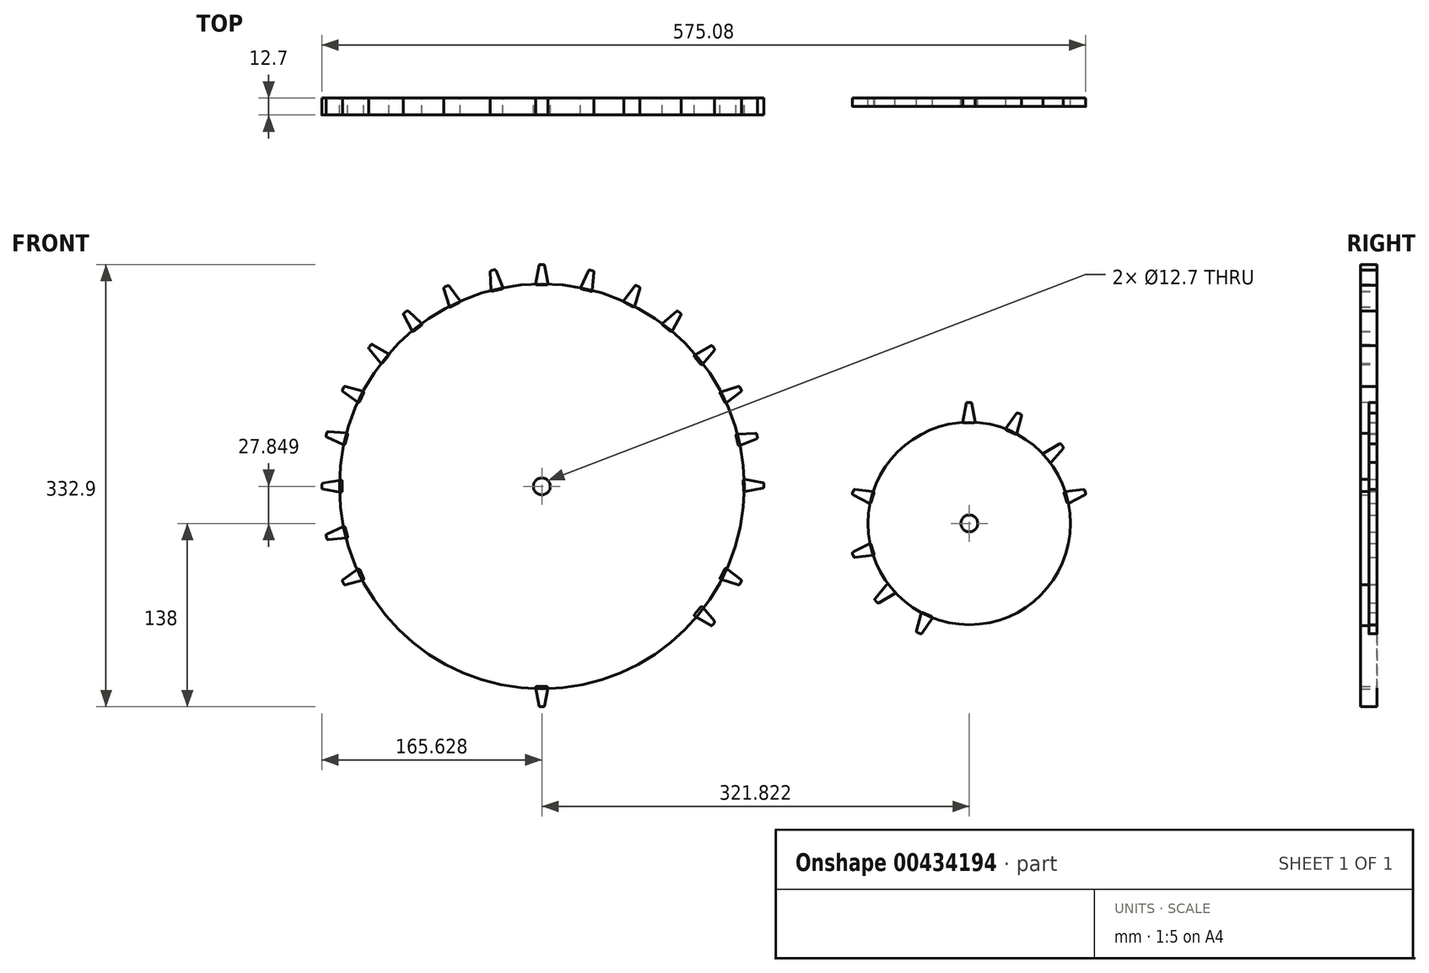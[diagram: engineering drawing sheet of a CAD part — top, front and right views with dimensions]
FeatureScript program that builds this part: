
annotation { "Feature Type Name" : "Feature", "Feature Type Description" : "" }
export const myFeature = defineFeature(function(context is Context, id is Id, definition is map)
    precondition{}
    {
        {
            var Q0;
            Q0=qCreatedBy(makeId("Front.planeOp"),FACE);
            var sketch = newSketch(context, id + "F0", { "sketchPlane" : qUnion([Q0])});
            skCircle(sketch, "E0", {"center": v(-44.38, 27.85) * mm, "radius": 152.4 * mm});
            skCircle(sketch, "E1", {"center": v(-44.38, 27.85) * mm, "radius": 6.35 * mm});
            skSolve(sketch);
        }
        {
            var Q0;
            Q0=qCreatedBy(makeId("Front.planeOp"),FACE);
            var sketch = newSketch(context, id + "F1", { "sketchPlane" : qUnion([Q0])});
            skCircle(sketch, "E2", {"center": v(277.44, 0) * mm, "radius": 76.2 * mm});
            skCircle(sketch, "E3", {"center": v(277.44, 0) * mm, "radius": 6.35 * mm});
            skSolve(sketch);
        }
        {
            var Q0;
            Q0=qCreatedBy(makeId("Front.planeOp"),FACE);
            var sketch = newSketch(context, id + "F2", { "sketchPlane" : qUnion([Q0])});
            skLineSegment(sketch, "E4.0", {"start": v(-40.88, 179.56) * mm, "end": v(-47.98, 179.5) * mm});
            skLineSegment(sketch, "E4.1", {"start": v(-48.96, 180.66) * mm, "end": v(-46.6, 194.09) * mm});
            skLineSegment(sketch, "E4.2", {"start": v(-45.63, 194.9) * mm, "end": v(-43.24, 194.9) * mm});
            skLineSegment(sketch, "E4.3", {"start": v(-42.27, 194.08) * mm, "end": v(-39.91, 180.72) * mm});
            skPoint(sketch, "E4.0.midPoint", {"position": v(-44.44, 179.53) * mm});
            skArc(sketch, "E5.filletArc", {"start": v(-45.63, 194.9) * mm, "mid": v(-46.26, 194.67) * mm, "end": v(-46.6, 194.09) * mm});
            skArc(sketch, "E6.filletArc", {"start": v(-42.27, 194.08) * mm, "mid": v(-42.6, 194.67) * mm, "end": v(-43.24, 194.9) * mm});
            skArc(sketch, "E7.filletArc", {"start": v(-48.96, 180.66) * mm, "mid": v(-48.74, 179.85) * mm, "end": v(-47.98, 179.5) * mm});
            skArc(sketch, "E8.filletArc", {"start": v(-40.88, 179.56) * mm, "mid": v(-40.12, 179.92) * mm, "end": v(-39.91, 180.72) * mm});
            skLineSegment(sketch, "E9.2.0", {"start": v(70.92, 126.83) * mm, "end": v(82.73, 133.64) * mm});
            skLineSegment(sketch, "E9.2.1", {"start": v(83.97, 133.42) * mm, "end": v(85.5, 131.6) * mm});
            skLineSegment(sketch, "E9.2.2", {"start": v(85.5, 130.32) * mm, "end": v(76.78, 119.93) * mm});
            skArc(sketch, "E9.2.3", {"start": v(70.92, 126.83) * mm, "mid": v(70.44, 126.14) * mm, "end": v(70.66, 125.32) * mm});
            skLineSegment(sketch, "E9.2.4", {"start": v(75.27, 119.93) * mm, "end": v(70.66, 125.32) * mm});
            skArc(sketch, "E9.2.5", {"start": v(75.27, 119.93) * mm, "mid": v(76.03, 119.58) * mm, "end": v(76.78, 119.93) * mm});
            skArc(sketch, "E9.2.6", {"start": v(85.5, 130.32) * mm, "mid": v(85.73, 130.96) * mm, "end": v(85.5, 131.6) * mm});
            skArc(sketch, "E9.2.7", {"start": v(83.97, 133.42) * mm, "mid": v(83.39, 133.76) * mm, "end": v(82.73, 133.64) * mm});
            skPoint(sketch, "E9.center", {"position": v(-44.45, 28.45) * mm});
            skLineSegment(sketch, "E10.0", {"start": v(-106.5, 166.2) * mm, "end": v(-112.83, 163) * mm});
            skLineSegment(sketch, "E10.1", {"start": v(-114.23, 163.6) * mm, "end": v(-118.08, 176.67) * mm});
            skLineSegment(sketch, "E10.2", {"start": v(-117.58, 177.83) * mm, "end": v(-115.44, 178.9) * mm});
            skLineSegment(sketch, "E10.3", {"start": v(-114.2, 178.6) * mm, "end": v(-106.15, 167.67) * mm});
            skArc(sketch, "E11.filletArc", {"start": v(-117.58, 177.83) * mm, "mid": v(-118.04, 177.34) * mm, "end": v(-118.08, 176.67) * mm});
            skArc(sketch, "E12.filletArc", {"start": v(-114.2, 178.6) * mm, "mid": v(-114.77, 178.97) * mm, "end": v(-115.44, 178.9) * mm});
            skArc(sketch, "E13.filletArc", {"start": v(-114.23, 163.6) * mm, "mid": v(-113.67, 162.97) * mm, "end": v(-112.83, 163) * mm});
            skArc(sketch, "E14.filletArc", {"start": v(-106.5, 166.2) * mm, "mid": v(-105.98, 166.86) * mm, "end": v(-106.15, 167.67) * mm});
            skLineSegment(sketch, "E15.2.0", {"start": v(46.7, 150.6) * mm, "end": v(56.96, 159.58) * mm});
            skLineSegment(sketch, "E15.2.1", {"start": v(58.22, 159.6) * mm, "end": v(60.08, 158.1) * mm});
            skLineSegment(sketch, "E15.2.2", {"start": v(60.32, 156.86) * mm, "end": v(53.78, 144.98) * mm});
            skArc(sketch, "E15.2.3", {"start": v(46.7, 150.6) * mm, "mid": v(46.35, 149.84) * mm, "end": v(46.73, 149.09) * mm});
            skLineSegment(sketch, "E15.2.4", {"start": v(52.3, 144.68) * mm, "end": v(46.73, 149.09) * mm});
            skArc(sketch, "E15.2.5", {"start": v(52.3, 144.68) * mm, "mid": v(53.1, 144.49) * mm, "end": v(53.78, 144.98) * mm});
            skArc(sketch, "E15.2.6", {"start": v(60.32, 156.86) * mm, "mid": v(60.43, 157.53) * mm, "end": v(60.08, 158.1) * mm});
            skArc(sketch, "E15.2.7", {"start": v(58.22, 159.6) * mm, "mid": v(57.58, 159.82) * mm, "end": v(56.96, 159.58) * mm});
            skLineSegment(sketch, "E16.0", {"start": v(-135.04, 149.13) * mm, "end": v(-140.62, 144.74) * mm});
            skLineSegment(sketch, "E16.1", {"start": v(-142.1, 145.06) * mm, "end": v(-148.45, 157.12) * mm});
            skLineSegment(sketch, "E16.2", {"start": v(-148.18, 158.36) * mm, "end": v(-146.3, 159.82) * mm});
            skLineSegment(sketch, "E16.3", {"start": v(-145.02, 159.77) * mm, "end": v(-134.99, 150.64) * mm});
            skArc(sketch, "E17.filletArc", {"start": v(-148.18, 158.36) * mm, "mid": v(-148.54, 157.79) * mm, "end": v(-148.45, 157.12) * mm});
            skArc(sketch, "E18.filletArc", {"start": v(-145.02, 159.77) * mm, "mid": v(-145.65, 160.02) * mm, "end": v(-146.3, 159.82) * mm});
            skArc(sketch, "E19.filletArc", {"start": v(-142.1, 145.06) * mm, "mid": v(-141.43, 144.55) * mm, "end": v(-140.62, 144.74) * mm});
            skArc(sketch, "E20.filletArc", {"start": v(-135.04, 149.13) * mm, "mid": v(-134.66, 149.88) * mm, "end": v(-134.99, 150.64) * mm});
            skLineSegment(sketch, "E21.2.0", {"start": v(90.49, 98.98) * mm, "end": v(103.49, 103.08) * mm});
            skLineSegment(sketch, "E21.2.1", {"start": v(104.65, 102.6) * mm, "end": v(105.76, 100.48) * mm});
            skLineSegment(sketch, "E21.2.2", {"start": v(105.48, 99.23) * mm, "end": v(94.72, 90.98) * mm});
            skArc(sketch, "E21.2.3", {"start": v(90.49, 98.98) * mm, "mid": v(89.87, 98.4) * mm, "end": v(89.91, 97.57) * mm});
            skLineSegment(sketch, "E21.2.4", {"start": v(93.24, 91.3) * mm, "end": v(89.91, 97.57) * mm});
            skArc(sketch, "E21.2.5", {"start": v(93.24, 91.3) * mm, "mid": v(93.9, 90.8) * mm, "end": v(94.72, 90.98) * mm});
            skArc(sketch, "E21.2.6", {"start": v(105.48, 99.23) * mm, "mid": v(105.85, 99.8) * mm, "end": v(105.76, 100.48) * mm});
            skArc(sketch, "E21.2.7", {"start": v(104.65, 102.6) * mm, "mid": v(104.16, 103.05) * mm, "end": v(103.49, 103.08) * mm});
            skLineSegment(sketch, "E22.0", {"start": v(-74.46, 176.41) * mm, "end": v(-81.38, 174.8) * mm});
            skLineSegment(sketch, "E22.1", {"start": v(-82.59, 175.73) * mm, "end": v(-83.2, 189.35) * mm});
            skLineSegment(sketch, "E22.2", {"start": v(-82.43, 190.35) * mm, "end": v(-80.1, 190.87) * mm});
            skLineSegment(sketch, "E22.3", {"start": v(-78.97, 190.28) * mm, "end": v(-73.77, 177.76) * mm});
            skArc(sketch, "E23.filletArc", {"start": v(-82.43, 190.35) * mm, "mid": v(-83, 190) * mm, "end": v(-83.2, 189.35) * mm});
            skArc(sketch, "E24.filletArc", {"start": v(-78.97, 190.28) * mm, "mid": v(-79.43, 190.78) * mm, "end": v(-80.1, 190.87) * mm});
            skArc(sketch, "E25.filletArc", {"start": v(-82.59, 175.73) * mm, "mid": v(-82.2, 174.98) * mm, "end": v(-81.38, 174.8) * mm});
            skArc(sketch, "E26.filletArc", {"start": v(-74.46, 176.41) * mm, "mid": v(-73.8, 176.93) * mm, "end": v(-73.77, 177.76) * mm});
            skLineSegment(sketch, "E27.2.0", {"start": v(17.42, 167.9) * mm, "end": v(25.67, 178.74) * mm});
            skLineSegment(sketch, "E27.2.1", {"start": v(26.9, 179.02) * mm, "end": v(29.02, 177.93) * mm});
            skLineSegment(sketch, "E27.2.2", {"start": v(29.52, 176.75) * mm, "end": v(25.5, 163.8) * mm});
            skArc(sketch, "E27.2.3", {"start": v(17.42, 167.9) * mm, "mid": v(17.24, 167.07) * mm, "end": v(17.76, 166.4) * mm});
            skLineSegment(sketch, "E27.2.4", {"start": v(24.1, 163.2) * mm, "end": v(17.76, 166.4) * mm});
            skArc(sketch, "E27.2.5", {"start": v(24.1, 163.2) * mm, "mid": v(24.93, 163.18) * mm, "end": v(25.5, 163.8) * mm});
            skArc(sketch, "E27.2.6", {"start": v(29.52, 176.75) * mm, "mid": v(29.48, 177.43) * mm, "end": v(29.02, 177.93) * mm});
            skArc(sketch, "E27.2.7", {"start": v(26.9, 179.02) * mm, "mid": v(26.24, 179.1) * mm, "end": v(25.67, 178.74) * mm});
            skLineSegment(sketch, "E28.2.0", {"start": v(305.15, 71.5) * mm, "end": v(312.9, 82.72) * mm});
            skLineSegment(sketch, "E28.2.1", {"start": v(314.1, 83.06) * mm, "end": v(316.28, 82.06) * mm});
            skLineSegment(sketch, "E28.2.2", {"start": v(316.82, 80.91) * mm, "end": v(313.4, 67.79) * mm});
            skArc(sketch, "E28.2.3", {"start": v(305.15, 71.5) * mm, "mid": v(305.01, 70.67) * mm, "end": v(305.56, 70.03) * mm});
            skLineSegment(sketch, "E28.2.4", {"start": v(312.04, 67.13) * mm, "end": v(305.56, 70.03) * mm});
            skArc(sketch, "E28.2.5", {"start": v(312.04, 67.13) * mm, "mid": v(312.87, 67.15) * mm, "end": v(313.4, 67.79) * mm});
            skArc(sketch, "E28.2.6", {"start": v(316.82, 80.91) * mm, "mid": v(316.76, 81.59) * mm, "end": v(316.28, 82.06) * mm});
            skArc(sketch, "E28.2.7", {"start": v(314.1, 83.06) * mm, "mid": v(313.44, 83.11) * mm, "end": v(312.9, 82.72) * mm});
            skLineSegment(sketch, "E29.2.0", {"start": v(333.52, 53) * mm, "end": v(345.33, 59.81) * mm});
            skLineSegment(sketch, "E29.2.1", {"start": v(346.57, 59.6) * mm, "end": v(348.1, 57.76) * mm});
            skLineSegment(sketch, "E29.2.2", {"start": v(348.1, 56.5) * mm, "end": v(339.38, 46.1) * mm});
            skArc(sketch, "E29.2.3", {"start": v(333.52, 53) * mm, "mid": v(333.04, 52.3) * mm, "end": v(333.26, 51.5) * mm});
            skLineSegment(sketch, "E29.2.4", {"start": v(337.87, 46.1) * mm, "end": v(333.26, 51.5) * mm});
            skArc(sketch, "E29.2.5", {"start": v(337.87, 46.1) * mm, "mid": v(338.63, 45.75) * mm, "end": v(339.38, 46.1) * mm});
            skArc(sketch, "E29.2.6", {"start": v(348.1, 56.5) * mm, "mid": v(348.33, 57.13) * mm, "end": v(348.1, 57.76) * mm});
            skArc(sketch, "E29.2.7", {"start": v(346.57, 59.6) * mm, "mid": v(345.99, 59.93) * mm, "end": v(345.33, 59.81) * mm});
            skLineSegment(sketch, "E30.2.0", {"start": v(272.67, 76.78) * mm, "end": v(275.03, 90.2) * mm});
            skLineSegment(sketch, "E30.2.1", {"start": v(276, 91.02) * mm, "end": v(278.39, 91.02) * mm});
            skLineSegment(sketch, "E30.2.2", {"start": v(279.36, 90.2) * mm, "end": v(281.72, 76.84) * mm});
            skArc(sketch, "E30.2.3", {"start": v(272.67, 76.78) * mm, "mid": v(272.89, 75.97) * mm, "end": v(273.65, 75.62) * mm});
            skLineSegment(sketch, "E30.2.4", {"start": v(280.75, 75.68) * mm, "end": v(273.65, 75.62) * mm});
            skArc(sketch, "E30.2.5", {"start": v(280.75, 75.68) * mm, "mid": v(281.5, 76.04) * mm, "end": v(281.72, 76.84) * mm});
            skArc(sketch, "E30.2.6", {"start": v(279.36, 90.2) * mm, "mid": v(279.02, 90.78) * mm, "end": v(278.39, 91.02) * mm});
            skArc(sketch, "E30.2.7", {"start": v(276, 91.02) * mm, "mid": v(275.37, 90.79) * mm, "end": v(275.03, 90.2) * mm});
            skLineSegment(sketch, "E31.2.0", {"start": v(-195.78, 23.52) * mm, "end": v(-209.2, 25.88) * mm});
            skLineSegment(sketch, "E31.2.1", {"start": v(-210.01, 26.85) * mm, "end": v(-210.01, 29.24) * mm});
            skLineSegment(sketch, "E31.2.2", {"start": v(-209.2, 30.21) * mm, "end": v(-195.84, 32.57) * mm});
            skArc(sketch, "E31.2.3", {"start": v(-195.78, 23.52) * mm, "mid": v(-194.96, 23.74) * mm, "end": v(-194.61, 24.5) * mm});
            skLineSegment(sketch, "E31.2.4", {"start": v(-194.67, 31.6) * mm, "end": v(-194.61, 24.5) * mm});
            skArc(sketch, "E31.2.5", {"start": v(-194.67, 31.6) * mm, "mid": v(-195.03, 32.35) * mm, "end": v(-195.84, 32.57) * mm});
            skArc(sketch, "E31.2.6", {"start": v(-209.2, 30.21) * mm, "mid": v(-209.78, 29.87) * mm, "end": v(-210.01, 29.24) * mm});
            skArc(sketch, "E31.2.7", {"start": v(-210.01, 26.85) * mm, "mid": v(-209.78, 26.22) * mm, "end": v(-209.2, 25.88) * mm});
            skLineSegment(sketch, "E32.0", {"start": v(-7.6, 174.65) * mm, "end": v(-14.46, 176.43) * mm});
            skLineSegment(sketch, "E32.1", {"start": v(-15.11, 177.8) * mm, "end": v(-9.35, 190.16) * mm});
            skLineSegment(sketch, "E32.2", {"start": v(-8.2, 190.7) * mm, "end": v(-5.9, 190.08) * mm});
            skLineSegment(sketch, "E32.3", {"start": v(-5.17, 189.04) * mm, "end": v(-6.36, 175.52) * mm});
            skArc(sketch, "E33.filletArc", {"start": v(-8.2, 190.7) * mm, "mid": v(-8.88, 190.64) * mm, "end": v(-9.35, 190.16) * mm});
            skArc(sketch, "E34.filletArc", {"start": v(-5.17, 189.04) * mm, "mid": v(-5.35, 189.7) * mm, "end": v(-5.9, 190.08) * mm});
            skArc(sketch, "E35.filletArc", {"start": v(-15.11, 177.8) * mm, "mid": v(-15.11, 176.97) * mm, "end": v(-14.46, 176.43) * mm});
            skArc(sketch, "E36.filletArc", {"start": v(-7.6, 174.65) * mm, "mid": v(-6.77, 174.8) * mm, "end": v(-6.36, 175.52) * mm});
            skLineSegment(sketch, "E37.2.0", {"start": v(-193.86, 59.21) * mm, "end": v(-206.22, 64.98) * mm});
            skLineSegment(sketch, "E37.2.1", {"start": v(-206.75, 66.12) * mm, "end": v(-206.13, 68.42) * mm});
            skLineSegment(sketch, "E37.2.2", {"start": v(-205.1, 69.15) * mm, "end": v(-191.58, 67.97) * mm});
            skArc(sketch, "E37.2.3", {"start": v(-193.86, 59.21) * mm, "mid": v(-193.02, 59.22) * mm, "end": v(-192.49, 59.86) * mm});
            skLineSegment(sketch, "E37.2.4", {"start": v(-190.7, 66.74) * mm, "end": v(-192.49, 59.86) * mm});
            skArc(sketch, "E37.2.5", {"start": v(-190.7, 66.74) * mm, "mid": v(-190.86, 67.56) * mm, "end": v(-191.58, 67.97) * mm});
            skArc(sketch, "E37.2.6", {"start": v(-205.1, 69.15) * mm, "mid": v(-205.75, 68.98) * mm, "end": v(-206.13, 68.42) * mm});
            skArc(sketch, "E37.2.7", {"start": v(-206.75, 66.12) * mm, "mid": v(-206.7, 65.45) * mm, "end": v(-206.22, 64.98) * mm});
            skLineSegment(sketch, "E38.0", {"start": v(-159.8, 126.2) * mm, "end": v(-164.36, 120.76) * mm});
            skLineSegment(sketch, "E38.1", {"start": v(-165.88, 120.77) * mm, "end": v(-174.55, 131.3) * mm});
            skLineSegment(sketch, "E38.2", {"start": v(-174.54, 132.55) * mm, "end": v(-173, 134.37) * mm});
            skLineSegment(sketch, "E38.3", {"start": v(-171.73, 134.58) * mm, "end": v(-160.05, 127.7) * mm});
            skArc(sketch, "E39.filletArc", {"start": v(-174.54, 132.55) * mm, "mid": v(-174.78, 131.92) * mm, "end": v(-174.55, 131.3) * mm});
            skArc(sketch, "E40.filletArc", {"start": v(-171.73, 134.58) * mm, "mid": v(-172.4, 134.7) * mm, "end": v(-173, 134.37) * mm});
            skArc(sketch, "E41.filletArc", {"start": v(-165.88, 120.77) * mm, "mid": v(-165.12, 120.4) * mm, "end": v(-164.36, 120.76) * mm});
            skArc(sketch, "E42.filletArc", {"start": v(-159.8, 126.2) * mm, "mid": v(-159.57, 127) * mm, "end": v(-160.05, 127.7) * mm});
            skLineSegment(sketch, "E43.2.0", {"start": v(349.74, 23.87) * mm, "end": v(363.27, 25.55) * mm});
            skLineSegment(sketch, "E43.2.1", {"start": v(364.32, 24.86) * mm, "end": v(365.02, 22.58) * mm});
            skLineSegment(sketch, "E43.2.2", {"start": v(364.53, 21.4) * mm, "end": v(352.45, 15.24) * mm});
            skArc(sketch, "E43.2.3", {"start": v(349.74, 23.87) * mm, "mid": v(349.02, 23.42) * mm, "end": v(348.91, 22.59) * mm});
            skLineSegment(sketch, "E43.2.4", {"start": v(351.05, 15.82) * mm, "end": v(348.91, 22.59) * mm});
            skArc(sketch, "E43.2.5", {"start": v(351.05, 15.82) * mm, "mid": v(351.62, 15.2) * mm, "end": v(352.45, 15.24) * mm});
            skArc(sketch, "E43.2.6", {"start": v(364.53, 21.4) * mm, "mid": v(364.99, 21.9) * mm, "end": v(365.02, 22.58) * mm});
            skArc(sketch, "E43.2.7", {"start": v(364.32, 24.86) * mm, "mid": v(363.92, 25.4) * mm, "end": v(363.27, 25.55) * mm});
            skLineSegment(sketch, "E44.0", {"start": v(-178.5, 98.25) * mm, "end": v(-181.44, 91.79) * mm});
            skLineSegment(sketch, "E44.1", {"start": v(-182.91, 91.39) * mm, "end": v(-194.08, 99.2) * mm});
            skLineSegment(sketch, "E44.2", {"start": v(-194.4, 100.43) * mm, "end": v(-193.4, 102.59) * mm});
            skLineSegment(sketch, "E44.3", {"start": v(-192.24, 103.13) * mm, "end": v(-179.14, 99.62) * mm});
            skArc(sketch, "E45.filletArc", {"start": v(-194.4, 100.43) * mm, "mid": v(-194.47, 99.76) * mm, "end": v(-194.08, 99.2) * mm});
            skArc(sketch, "E46.filletArc", {"start": v(-192.24, 103.13) * mm, "mid": v(-192.92, 103.07) * mm, "end": v(-193.4, 102.59) * mm});
            skArc(sketch, "E47.filletArc", {"start": v(-182.91, 91.39) * mm, "mid": v(-182.08, 91.24) * mm, "end": v(-181.44, 91.79) * mm});
            skArc(sketch, "E48.filletArc", {"start": v(-178.5, 98.25) * mm, "mid": v(-178.5, 99.08) * mm, "end": v(-179.14, 99.62) * mm});
            skLineSegment(sketch, "E49.2.0", {"start": v(108.48, 33.17) * mm, "end": v(121.9, 30.8) * mm});
            skLineSegment(sketch, "E49.2.1", {"start": v(122.72, 29.84) * mm, "end": v(122.72, 27.45) * mm});
            skLineSegment(sketch, "E49.2.2", {"start": v(121.9, 26.48) * mm, "end": v(108.54, 24.12) * mm});
            skArc(sketch, "E49.2.3", {"start": v(108.48, 33.17) * mm, "mid": v(107.67, 32.95) * mm, "end": v(107.32, 32.19) * mm});
            skLineSegment(sketch, "E49.2.4", {"start": v(107.38, 25.09) * mm, "end": v(107.32, 32.19) * mm});
            skArc(sketch, "E49.2.5", {"start": v(107.38, 25.09) * mm, "mid": v(107.74, 24.33) * mm, "end": v(108.54, 24.12) * mm});
            skArc(sketch, "E49.2.6", {"start": v(121.9, 26.48) * mm, "mid": v(122.49, 26.81) * mm, "end": v(122.72, 27.45) * mm});
            skArc(sketch, "E49.2.7", {"start": v(122.72, 29.84) * mm, "mid": v(122.5, 30.47) * mm, "end": v(121.9, 30.8) * mm});
            skLineSegment(sketch, "E50.2.0", {"start": v(102.7, 67.32) * mm, "end": v(116.33, 67.88) * mm});
            skLineSegment(sketch, "E50.2.1", {"start": v(117.33, 67.11) * mm, "end": v(117.84, 64.78) * mm});
            skLineSegment(sketch, "E50.2.2", {"start": v(117.25, 63.65) * mm, "end": v(104.7, 58.5) * mm});
            skArc(sketch, "E50.2.3", {"start": v(102.7, 67.32) * mm, "mid": v(101.96, 66.93) * mm, "end": v(101.78, 66.11) * mm});
            skLineSegment(sketch, "E50.2.4", {"start": v(103.36, 59.19) * mm, "end": v(101.78, 66.11) * mm});
            skArc(sketch, "E50.2.5", {"start": v(103.36, 59.19) * mm, "mid": v(103.87, 58.53) * mm, "end": v(104.7, 58.5) * mm});
            skArc(sketch, "E50.2.6", {"start": v(117.25, 63.65) * mm, "mid": v(117.75, 64.11) * mm, "end": v(117.84, 64.78) * mm});
            skArc(sketch, "E50.2.7", {"start": v(117.33, 67.11) * mm, "mid": v(116.97, 67.68) * mm, "end": v(116.33, 67.88) * mm});
            skLineSegment(sketch, "E51.MirrorCS", {"start": v(-42.27, -137.18) * mm, "end": v(-39.91, -123.83) * mm});
            skLineSegment(sketch, "E52.MirrorCS", {"start": v(-48.96, -123.76) * mm, "end": v(-46.6, -137.2) * mm});
            skLineSegment(sketch, "E53.MirrorCS", {"start": v(-45.63, -138) * mm, "end": v(-43.24, -138) * mm});
            skArc(sketch, "E54.MirrorCS", {"start": v(-45.63, -138) * mm, "mid": v(-46.26, -137.77) * mm, "end": v(-46.6, -137.2) * mm});
            skArc(sketch, "E55.MirrorCS", {"start": v(-42.27, -137.18) * mm, "mid": v(-42.6, -137.77) * mm, "end": v(-43.24, -138) * mm});
            skLineSegment(sketch, "E56.MirrorCS", {"start": v(-40.88, -122.66) * mm, "end": v(-47.98, -122.6) * mm});
            skArc(sketch, "E57.MirrorCS", {"start": v(-40.88, -122.66) * mm, "mid": v(-40.12, -123.02) * mm, "end": v(-39.91, -123.83) * mm});
            skArc(sketch, "E58.MirrorCS", {"start": v(-48.96, -123.76) * mm, "mid": v(-48.74, -122.95) * mm, "end": v(-47.98, -122.6) * mm});
            skArc(sketch, "E59.MirrorCS", {"start": v(-78.97, -133.39) * mm, "mid": v(-79.43, -133.89) * mm, "end": v(-80.1, -133.97) * mm});
            skLineSegment(sketch, "E60.MirrorCS", {"start": v(-82.43, -133.46) * mm, "end": v(-80.1, -133.97) * mm});
            skArc(sketch, "E61.MirrorCS", {"start": v(-82.43, -133.46) * mm, "mid": v(-83, -133.1) * mm, "end": v(-83.2, -132.45) * mm});
            skLineSegment(sketch, "E62.MirrorCS", {"start": v(-82.59, -118.83) * mm, "end": v(-83.2, -132.45) * mm});
            skArc(sketch, "E63.MirrorCS", {"start": v(-82.59, -118.83) * mm, "mid": v(-82.2, -118.09) * mm, "end": v(-81.38, -117.91) * mm});
            skLineSegment(sketch, "E64.MirrorCS", {"start": v(-74.46, -119.52) * mm, "end": v(-81.38, -117.91) * mm});
            skArc(sketch, "E65.MirrorCS", {"start": v(-74.46, -119.52) * mm, "mid": v(-73.8, -120.03) * mm, "end": v(-73.77, -120.86) * mm});
            skLineSegment(sketch, "E66.MirrorCS", {"start": v(-78.97, -133.39) * mm, "end": v(-73.77, -120.86) * mm});
            skArc(sketch, "E67.MirrorCS", {"start": v(-114.2, -121.7) * mm, "mid": v(-114.77, -122.07) * mm, "end": v(-115.44, -122) * mm});
            skLineSegment(sketch, "E68.MirrorCS", {"start": v(-117.58, -120.93) * mm, "end": v(-115.44, -122) * mm});
            skArc(sketch, "E69.MirrorCS", {"start": v(-117.58, -120.93) * mm, "mid": v(-118.04, -120.45) * mm, "end": v(-118.08, -119.78) * mm});
            skLineSegment(sketch, "E70.MirrorCS", {"start": v(-114.23, -106.7) * mm, "end": v(-118.08, -119.78) * mm});
            skArc(sketch, "E71.MirrorCS", {"start": v(-114.23, -106.7) * mm, "mid": v(-113.67, -106.07) * mm, "end": v(-112.83, -106.1) * mm});
            skLineSegment(sketch, "E72.MirrorCS", {"start": v(-106.5, -109.3) * mm, "end": v(-112.83, -106.1) * mm});
            skArc(sketch, "E73.MirrorCS", {"start": v(-106.5, -109.3) * mm, "mid": v(-105.98, -109.96) * mm, "end": v(-106.15, -110.78) * mm});
            skLineSegment(sketch, "E74.MirrorCS", {"start": v(-114.2, -121.7) * mm, "end": v(-106.15, -110.78) * mm});
            skArc(sketch, "E75.MirrorCS", {"start": v(-145.02, -102.87) * mm, "mid": v(-145.65, -103.13) * mm, "end": v(-146.3, -102.92) * mm});
            skLineSegment(sketch, "E76.MirrorCS", {"start": v(-148.18, -101.46) * mm, "end": v(-146.3, -102.92) * mm});
            skArc(sketch, "E77.MirrorCS", {"start": v(-148.18, -101.46) * mm, "mid": v(-148.54, -100.9) * mm, "end": v(-148.45, -100.23) * mm});
            skLineSegment(sketch, "E78.MirrorCS", {"start": v(-142.1, -88.16) * mm, "end": v(-148.45, -100.23) * mm});
            skArc(sketch, "E79.MirrorCS", {"start": v(-142.1, -88.16) * mm, "mid": v(-141.43, -87.65) * mm, "end": v(-140.62, -87.84) * mm});
            skLineSegment(sketch, "E80.MirrorCS", {"start": v(-135.04, -92.24) * mm, "end": v(-140.62, -87.84) * mm});
            skArc(sketch, "E81.MirrorCS", {"start": v(-135.04, -92.24) * mm, "mid": v(-134.66, -92.98) * mm, "end": v(-134.99, -93.75) * mm});
            skLineSegment(sketch, "E82.MirrorCS", {"start": v(-145.02, -102.87) * mm, "end": v(-134.99, -93.75) * mm});
            skArc(sketch, "E83.MirrorCS", {"start": v(-171.73, -77.68) * mm, "mid": v(-172.4, -77.8) * mm, "end": v(-173, -77.47) * mm});
            skLineSegment(sketch, "E84.MirrorCS", {"start": v(-174.54, -75.66) * mm, "end": v(-173, -77.47) * mm});
            skArc(sketch, "E85.MirrorCS", {"start": v(-174.54, -75.66) * mm, "mid": v(-174.78, -75.03) * mm, "end": v(-174.55, -74.4) * mm});
            skLineSegment(sketch, "E86.MirrorCS", {"start": v(-165.88, -63.87) * mm, "end": v(-174.55, -74.4) * mm});
            skArc(sketch, "E87.MirrorCS", {"start": v(-165.88, -63.87) * mm, "mid": v(-165.12, -63.51) * mm, "end": v(-164.36, -63.87) * mm});
            skLineSegment(sketch, "E88.MirrorCS", {"start": v(-159.8, -69.3) * mm, "end": v(-164.36, -63.87) * mm});
            skArc(sketch, "E89.MirrorCS", {"start": v(-159.8, -69.3) * mm, "mid": v(-159.57, -70.11) * mm, "end": v(-160.05, -70.8) * mm});
            skLineSegment(sketch, "E90.MirrorCS", {"start": v(-171.73, -77.68) * mm, "end": v(-160.05, -70.8) * mm});
            skLineSegment(sketch, "E91.MirrorCS", {"start": v(-182.91, -34.5) * mm, "end": v(-194.08, -42.31) * mm});
            skArc(sketch, "E92.MirrorCS", {"start": v(-194.4, -43.53) * mm, "mid": v(-194.47, -42.86) * mm, "end": v(-194.08, -42.31) * mm});
            skLineSegment(sketch, "E93.MirrorCS", {"start": v(-194.4, -43.53) * mm, "end": v(-193.4, -45.7) * mm});
            skArc(sketch, "E94.MirrorCS", {"start": v(-192.24, -46.23) * mm, "mid": v(-192.92, -46.17) * mm, "end": v(-193.4, -45.7) * mm});
            skLineSegment(sketch, "E95.MirrorCS", {"start": v(-192.24, -46.23) * mm, "end": v(-179.14, -42.72) * mm});
            skArc(sketch, "E96.MirrorCS", {"start": v(-178.5, -41.35) * mm, "mid": v(-178.5, -42.19) * mm, "end": v(-179.14, -42.72) * mm});
            skLineSegment(sketch, "E97.MirrorCS", {"start": v(-178.5, -41.35) * mm, "end": v(-181.44, -34.9) * mm});
            skArc(sketch, "E98.MirrorCS", {"start": v(-182.91, -34.5) * mm, "mid": v(-182.08, -34.35) * mm, "end": v(-181.44, -34.9) * mm});
            skLineSegment(sketch, "E99.MirrorCS", {"start": v(-205.1, -12.26) * mm, "end": v(-191.58, -11.08) * mm});
            skArc(sketch, "E100.MirrorCS", {"start": v(-205.1, -12.26) * mm, "mid": v(-205.75, -12.08) * mm, "end": v(-206.13, -11.53) * mm});
            skLineSegment(sketch, "E101.MirrorCS", {"start": v(-206.75, -9.22) * mm, "end": v(-206.13, -11.53) * mm});
            skArc(sketch, "E102.MirrorCS", {"start": v(-206.75, -9.22) * mm, "mid": v(-206.7, -8.55) * mm, "end": v(-206.22, -8.08) * mm});
            skLineSegment(sketch, "E103.MirrorCS", {"start": v(-193.86, -2.32) * mm, "end": v(-206.22, -8.08) * mm});
            skArc(sketch, "E104.MirrorCS", {"start": v(-193.86, -2.32) * mm, "mid": v(-193.02, -2.32) * mm, "end": v(-192.49, -2.97) * mm});
            skLineSegment(sketch, "E105.MirrorCS", {"start": v(-190.7, -9.84) * mm, "end": v(-192.49, -2.97) * mm});
            skArc(sketch, "E106.MirrorCS", {"start": v(-190.7, -9.84) * mm, "mid": v(-190.86, -10.66) * mm, "end": v(-191.58, -11.08) * mm});
            skArc(sketch, "E107.MirrorCS", {"start": v(-8.2, -133.8) * mm, "mid": v(-8.88, -133.74) * mm, "end": v(-9.35, -133.27) * mm});
            skLineSegment(sketch, "E108.MirrorCS", {"start": v(-15.11, -120.91) * mm, "end": v(-9.35, -133.27) * mm});
            skLineSegment(sketch, "E109.MirrorCS", {"start": v(-8.2, -133.8) * mm, "end": v(-5.9, -133.18) * mm});
            skArc(sketch, "E110.MirrorCS", {"start": v(-5.17, -132.14) * mm, "mid": v(-5.35, -132.8) * mm, "end": v(-5.9, -133.18) * mm});
            skLineSegment(sketch, "E111.MirrorCS", {"start": v(-5.17, -132.14) * mm, "end": v(-6.36, -118.63) * mm});
            skArc(sketch, "E112.MirrorCS", {"start": v(-15.11, -120.91) * mm, "mid": v(-15.11, -120.07) * mm, "end": v(-14.46, -119.53) * mm});
            skLineSegment(sketch, "E113.MirrorCS", {"start": v(-7.6, -117.76) * mm, "end": v(-14.46, -119.53) * mm});
            skArc(sketch, "E114.MirrorCS", {"start": v(-7.6, -117.76) * mm, "mid": v(-6.77, -117.9) * mm, "end": v(-6.36, -118.63) * mm});
            skArc(sketch, "E115.MirrorCS", {"start": v(26.9, -122.12) * mm, "mid": v(26.24, -122.2) * mm, "end": v(25.67, -121.85) * mm});
            skLineSegment(sketch, "E116.MirrorCS", {"start": v(17.42, -111) * mm, "end": v(25.67, -121.85) * mm});
            skLineSegment(sketch, "E117.MirrorCS", {"start": v(26.9, -122.12) * mm, "end": v(29.02, -121.03) * mm});
            skArc(sketch, "E118.MirrorCS", {"start": v(29.52, -119.86) * mm, "mid": v(29.48, -120.53) * mm, "end": v(29.02, -121.03) * mm});
            skLineSegment(sketch, "E119.MirrorCS", {"start": v(29.52, -119.86) * mm, "end": v(25.5, -106.9) * mm});
            skArc(sketch, "E120.MirrorCS", {"start": v(17.42, -111) * mm, "mid": v(17.24, -110.17) * mm, "end": v(17.76, -109.51) * mm});
            skLineSegment(sketch, "E121.MirrorCS", {"start": v(24.1, -106.31) * mm, "end": v(17.76, -109.51) * mm});
            skArc(sketch, "E122.MirrorCS", {"start": v(24.1, -106.31) * mm, "mid": v(24.93, -106.29) * mm, "end": v(25.5, -106.9) * mm});
            skArc(sketch, "E123.MirrorCS", {"start": v(52.3, -87.78) * mm, "mid": v(53.1, -87.6) * mm, "end": v(53.78, -88.08) * mm});
            skLineSegment(sketch, "E124.MirrorCS", {"start": v(58.22, -102.7) * mm, "end": v(60.08, -101.21) * mm});
            skArc(sketch, "E125.MirrorCS", {"start": v(60.32, -99.96) * mm, "mid": v(60.43, -100.63) * mm, "end": v(60.08, -101.21) * mm});
            skArc(sketch, "E126.MirrorCS", {"start": v(46.7, -93.71) * mm, "mid": v(46.35, -92.94) * mm, "end": v(46.73, -92.2) * mm});
            skArc(sketch, "E127.MirrorCS", {"start": v(58.22, -102.7) * mm, "mid": v(57.58, -102.93) * mm, "end": v(56.96, -102.68) * mm});
            skLineSegment(sketch, "E128.MirrorCS", {"start": v(52.3, -87.78) * mm, "end": v(46.73, -92.2) * mm});
            skLineSegment(sketch, "E129.MirrorCS", {"start": v(60.32, -99.96) * mm, "end": v(53.78, -88.08) * mm});
            skLineSegment(sketch, "E130.MirrorCS", {"start": v(46.7, -93.71) * mm, "end": v(56.96, -102.68) * mm});
            skLineSegment(sketch, "E131.MirrorCS", {"start": v(70.92, -69.93) * mm, "end": v(82.73, -76.75) * mm});
            skArc(sketch, "E132.MirrorCS", {"start": v(70.92, -69.93) * mm, "mid": v(70.44, -69.24) * mm, "end": v(70.66, -68.43) * mm});
            skLineSegment(sketch, "E133.MirrorCS", {"start": v(75.27, -63.03) * mm, "end": v(70.66, -68.43) * mm});
            skArc(sketch, "E134.MirrorCS", {"start": v(103.36, -2.3) * mm, "mid": v(103.87, -1.63) * mm, "end": v(104.7, -1.6) * mm});
            skLineSegment(sketch, "E135.MirrorCS", {"start": v(104.65, -45.7) * mm, "end": v(105.76, -43.58) * mm});
            skArc(sketch, "E136.MirrorCS", {"start": v(117.25, -6.76) * mm, "mid": v(117.75, -7.21) * mm, "end": v(117.84, -7.89) * mm});
            skLineSegment(sketch, "E137.MirrorCS", {"start": v(83.97, -76.53) * mm, "end": v(85.5, -74.7) * mm});
            skLineSegment(sketch, "E138.MirrorCS", {"start": v(103.36, -2.3) * mm, "end": v(101.78, -9.21) * mm});
            skLineSegment(sketch, "E139.MirrorCS", {"start": v(117.25, -6.76) * mm, "end": v(104.7, -1.6) * mm});
            skArc(sketch, "E140.MirrorCS", {"start": v(104.65, -45.7) * mm, "mid": v(104.16, -46.15) * mm, "end": v(103.49, -46.18) * mm});
            skLineSegment(sketch, "E141.MirrorCS", {"start": v(102.7, -10.42) * mm, "end": v(116.33, -10.99) * mm});
            skArc(sketch, "E142.MirrorCS", {"start": v(117.33, -10.22) * mm, "mid": v(116.97, -10.78) * mm, "end": v(116.33, -10.99) * mm});
            skLineSegment(sketch, "E143.MirrorCS", {"start": v(117.33, -10.22) * mm, "end": v(117.84, -7.89) * mm});
            skArc(sketch, "E144.MirrorCS", {"start": v(102.7, -10.42) * mm, "mid": v(101.96, -10.04) * mm, "end": v(101.78, -9.21) * mm});
            skArc(sketch, "E145.MirrorCS", {"start": v(105.48, -42.34) * mm, "mid": v(105.85, -42.9) * mm, "end": v(105.76, -43.58) * mm});
            skArc(sketch, "E146.MirrorCS", {"start": v(90.49, -42.08) * mm, "mid": v(89.87, -41.51) * mm, "end": v(89.91, -40.67) * mm});
            skArc(sketch, "E147.MirrorCS", {"start": v(83.97, -76.53) * mm, "mid": v(83.39, -76.86) * mm, "end": v(82.73, -76.75) * mm});
            skArc(sketch, "E148.MirrorCS", {"start": v(85.5, -73.43) * mm, "mid": v(85.73, -74.06) * mm, "end": v(85.5, -74.7) * mm});
            skLineSegment(sketch, "E149.MirrorCS", {"start": v(85.5, -73.43) * mm, "end": v(76.78, -63.04) * mm});
            skLineSegment(sketch, "E150.MirrorCS", {"start": v(105.48, -42.34) * mm, "end": v(94.72, -34.08) * mm});
            skLineSegment(sketch, "E151.MirrorCS", {"start": v(93.24, -34.4) * mm, "end": v(89.91, -40.67) * mm});
            skLineSegment(sketch, "E152.MirrorCS", {"start": v(90.49, -42.08) * mm, "end": v(103.49, -46.18) * mm});
            skArc(sketch, "E153.MirrorCS", {"start": v(93.24, -34.4) * mm, "mid": v(93.9, -33.9) * mm, "end": v(94.72, -34.08) * mm});
            skArc(sketch, "E154.MirrorCS", {"start": v(75.27, -63.03) * mm, "mid": v(76.03, -62.68) * mm, "end": v(76.78, -63.04) * mm});
            skArc(sketch, "E155.MirrorCS", {"start": v(237.78, 80.91) * mm, "mid": v(237.84, 81.59) * mm, "end": v(238.33, 82.06) * mm});
            skArc(sketch, "E156.MirrorCS", {"start": v(240.5, 83.06) * mm, "mid": v(241.17, 83.11) * mm, "end": v(241.71, 82.72) * mm});
            skLineSegment(sketch, "E157.MirrorCS", {"start": v(190.28, 24.86) * mm, "end": v(189.58, 22.58) * mm});
            skArc(sketch, "E158.MirrorCS", {"start": v(204.87, 23.87) * mm, "mid": v(205.58, 23.42) * mm, "end": v(205.7, 22.59) * mm});
            skArc(sketch, "E159.MirrorCS", {"start": v(221.09, 53) * mm, "mid": v(221.57, 52.3) * mm, "end": v(221.35, 51.5) * mm});
            skArc(sketch, "E160.MirrorCS", {"start": v(190.08, 21.4) * mm, "mid": v(189.62, 21.9) * mm, "end": v(189.58, 22.58) * mm});
            skArc(sketch, "E161.MirrorCS", {"start": v(190.28, 24.86) * mm, "mid": v(190.69, 25.4) * mm, "end": v(191.34, 25.55) * mm});
            skLineSegment(sketch, "E162.MirrorCS", {"start": v(240.5, 83.06) * mm, "end": v(238.33, 82.06) * mm});
            skArc(sketch, "E163.MirrorCS", {"start": v(242.56, 67.13) * mm, "mid": v(241.73, 67.15) * mm, "end": v(241.2, 67.79) * mm});
            skLineSegment(sketch, "E164.MirrorCS", {"start": v(208.04, 59.6) * mm, "end": v(206.5, 57.76) * mm});
            skLineSegment(sketch, "E165.MirrorCS", {"start": v(216.74, 46.1) * mm, "end": v(221.35, 51.5) * mm});
            skLineSegment(sketch, "E166.MirrorCS", {"start": v(203.55, 15.82) * mm, "end": v(205.7, 22.59) * mm});
            skArc(sketch, "E167.MirrorCS", {"start": v(216.74, 46.1) * mm, "mid": v(215.98, 45.75) * mm, "end": v(215.22, 46.1) * mm});
            skArc(sketch, "E168.MirrorCS", {"start": v(203.55, 15.82) * mm, "mid": v(202.99, 15.2) * mm, "end": v(202.16, 15.24) * mm});
            skArc(sketch, "E169.MirrorCS", {"start": v(206.5, 56.5) * mm, "mid": v(206.27, 57.13) * mm, "end": v(206.5, 57.76) * mm});
            skArc(sketch, "E170.MirrorCS", {"start": v(208.04, 59.6) * mm, "mid": v(208.62, 59.93) * mm, "end": v(209.28, 59.81) * mm});
            skArc(sketch, "E171.MirrorCS", {"start": v(249.46, 71.5) * mm, "mid": v(249.6, 70.67) * mm, "end": v(249.05, 70.03) * mm});
            skLineSegment(sketch, "E172.MirrorCS", {"start": v(242.56, 67.13) * mm, "end": v(249.05, 70.03) * mm});
            skLineSegment(sketch, "E173.MirrorCS", {"start": v(221.09, 53) * mm, "end": v(209.28, 59.81) * mm});
            skLineSegment(sketch, "E174.MirrorCS", {"start": v(204.87, 23.87) * mm, "end": v(191.34, 25.55) * mm});
            skLineSegment(sketch, "E175.MirrorCS", {"start": v(190.08, 21.4) * mm, "end": v(202.16, 15.24) * mm});
            skLineSegment(sketch, "E176.MirrorCS", {"start": v(206.5, 56.5) * mm, "end": v(215.22, 46.1) * mm});
            skLineSegment(sketch, "E177.MirrorCS", {"start": v(249.46, 71.5) * mm, "end": v(241.71, 82.72) * mm});
            skLineSegment(sketch, "E178.MirrorCS", {"start": v(237.78, 80.91) * mm, "end": v(241.2, 67.79) * mm});
            skArc(sketch, "E179.MirrorCS", {"start": v(190.08, -21.4) * mm, "mid": v(189.62, -21.9) * mm, "end": v(189.58, -22.58) * mm});
            skArc(sketch, "E180.MirrorCS", {"start": v(221.09, -53) * mm, "mid": v(221.57, -52.3) * mm, "end": v(221.35, -51.5) * mm});
            skArc(sketch, "E181.MirrorCS", {"start": v(204.87, -23.87) * mm, "mid": v(205.58, -23.42) * mm, "end": v(205.7, -22.59) * mm});
            skLineSegment(sketch, "E182.MirrorCS", {"start": v(190.28, -24.86) * mm, "end": v(189.58, -22.58) * mm});
            skArc(sketch, "E183.MirrorCS", {"start": v(208.04, -59.6) * mm, "mid": v(208.62, -59.93) * mm, "end": v(209.28, -59.81) * mm});
            skArc(sketch, "E184.MirrorCS", {"start": v(206.5, -56.5) * mm, "mid": v(206.27, -57.13) * mm, "end": v(206.5, -57.76) * mm});
            skArc(sketch, "E185.MirrorCS", {"start": v(216.74, -46.1) * mm, "mid": v(215.98, -45.75) * mm, "end": v(215.22, -46.1) * mm});
            skLineSegment(sketch, "E186.MirrorCS", {"start": v(216.74, -46.1) * mm, "end": v(221.35, -51.5) * mm});
            skLineSegment(sketch, "E187.MirrorCS", {"start": v(208.04, -59.6) * mm, "end": v(206.5, -57.76) * mm});
            skArc(sketch, "E188.MirrorCS", {"start": v(242.56, -67.13) * mm, "mid": v(241.73, -67.15) * mm, "end": v(241.2, -67.79) * mm});
            skArc(sketch, "E189.MirrorCS", {"start": v(190.28, -24.86) * mm, "mid": v(190.69, -25.4) * mm, "end": v(191.34, -25.55) * mm});
            skArc(sketch, "E190.MirrorCS", {"start": v(240.5, -83.06) * mm, "mid": v(241.17, -83.11) * mm, "end": v(241.71, -82.72) * mm});
            skLineSegment(sketch, "E191.MirrorCS", {"start": v(242.56, -67.13) * mm, "end": v(249.05, -70.03) * mm});
            skArc(sketch, "E192.MirrorCS", {"start": v(237.78, -80.91) * mm, "mid": v(237.84, -81.59) * mm, "end": v(238.33, -82.06) * mm});
            skArc(sketch, "E193.MirrorCS", {"start": v(249.46, -71.5) * mm, "mid": v(249.6, -70.67) * mm, "end": v(249.05, -70.03) * mm});
            skArc(sketch, "E194.MirrorCS", {"start": v(203.55, -15.82) * mm, "mid": v(202.99, -15.2) * mm, "end": v(202.16, -15.24) * mm});
            skLineSegment(sketch, "E195.MirrorCS", {"start": v(203.55, -15.82) * mm, "end": v(205.7, -22.59) * mm});
            skLineSegment(sketch, "E196.MirrorCS", {"start": v(240.5, -83.06) * mm, "end": v(238.33, -82.06) * mm});
            skLineSegment(sketch, "E197.MirrorCS", {"start": v(206.5, -56.5) * mm, "end": v(215.22, -46.1) * mm});
            skLineSegment(sketch, "E198.MirrorCS", {"start": v(190.08, -21.4) * mm, "end": v(202.16, -15.24) * mm});
            skLineSegment(sketch, "E199.MirrorCS", {"start": v(204.87, -23.87) * mm, "end": v(191.34, -25.55) * mm});
            skLineSegment(sketch, "E200.MirrorCS", {"start": v(221.09, -53) * mm, "end": v(209.28, -59.81) * mm});
            skLineSegment(sketch, "E201.MirrorCS", {"start": v(237.78, -80.91) * mm, "end": v(241.2, -67.79) * mm});
            skLineSegment(sketch, "E202.MirrorCS", {"start": v(249.46, -71.5) * mm, "end": v(241.71, -82.72) * mm});
            skArc(sketch, "E203.MirrorCS", {"start": v(364.53, -21.4) * mm, "mid": v(364.99, -21.9) * mm, "end": v(365.02, -22.58) * mm});
            skArc(sketch, "E204.MirrorCS", {"start": v(349.74, -23.87) * mm, "mid": v(349.02, -23.42) * mm, "end": v(348.91, -22.59) * mm});
            skLineSegment(sketch, "E205.MirrorCS", {"start": v(364.32, -24.86) * mm, "end": v(365.02, -22.58) * mm});
            skArc(sketch, "E206.MirrorCS", {"start": v(346.57, -59.6) * mm, "mid": v(345.99, -59.93) * mm, "end": v(345.33, -59.81) * mm});
            skArc(sketch, "E207.MirrorCS", {"start": v(348.1, -56.5) * mm, "mid": v(348.33, -57.13) * mm, "end": v(348.1, -57.76) * mm});
            skLineSegment(sketch, "E208.MirrorCS", {"start": v(346.57, -59.6) * mm, "end": v(348.1, -57.76) * mm});
            skArc(sketch, "E209.MirrorCS", {"start": v(364.32, -24.86) * mm, "mid": v(363.92, -25.4) * mm, "end": v(363.27, -25.55) * mm});
            skArc(sketch, "E210.MirrorCS", {"start": v(305.15, -71.5) * mm, "mid": v(305.01, -70.67) * mm, "end": v(305.56, -70.03) * mm});
            skArc(sketch, "E211.MirrorCS", {"start": v(351.05, -15.82) * mm, "mid": v(351.62, -15.2) * mm, "end": v(352.45, -15.24) * mm});
            skLineSegment(sketch, "E212.MirrorCS", {"start": v(351.05, -15.82) * mm, "end": v(348.91, -22.59) * mm});
            skLineSegment(sketch, "E213.MirrorCS", {"start": v(314.1, -83.06) * mm, "end": v(316.28, -82.06) * mm});
            skArc(sketch, "E214.MirrorCS", {"start": v(333.52, -53) * mm, "mid": v(333.04, -52.3) * mm, "end": v(333.26, -51.5) * mm});
            skArc(sketch, "E215.MirrorCS", {"start": v(337.87, -46.1) * mm, "mid": v(338.63, -45.75) * mm, "end": v(339.38, -46.1) * mm});
            skArc(sketch, "E216.MirrorCS", {"start": v(314.1, -83.06) * mm, "mid": v(313.44, -83.11) * mm, "end": v(312.9, -82.72) * mm});
            skArc(sketch, "E217.MirrorCS", {"start": v(316.82, -80.91) * mm, "mid": v(316.76, -81.59) * mm, "end": v(316.28, -82.06) * mm});
            skLineSegment(sketch, "E218.MirrorCS", {"start": v(333.52, -53) * mm, "end": v(345.33, -59.81) * mm});
            skLineSegment(sketch, "E219.MirrorCS", {"start": v(305.15, -71.5) * mm, "end": v(312.9, -82.72) * mm});
            skLineSegment(sketch, "E220.MirrorCS", {"start": v(337.87, -46.1) * mm, "end": v(333.26, -51.5) * mm});
            skArc(sketch, "E221.MirrorCS", {"start": v(312.04, -67.13) * mm, "mid": v(312.87, -67.15) * mm, "end": v(313.4, -67.79) * mm});
            skLineSegment(sketch, "E222.MirrorCS", {"start": v(312.04, -67.13) * mm, "end": v(305.56, -70.03) * mm});
            skLineSegment(sketch, "E223.MirrorCS", {"start": v(348.1, -56.5) * mm, "end": v(339.38, -46.1) * mm});
            skLineSegment(sketch, "E224.MirrorCS", {"start": v(364.53, -21.4) * mm, "end": v(352.45, -15.24) * mm});
            skLineSegment(sketch, "E225.MirrorCS", {"start": v(349.74, -23.87) * mm, "end": v(363.27, -25.55) * mm});
            skLineSegment(sketch, "E226.MirrorCS", {"start": v(316.82, -80.91) * mm, "end": v(313.4, -67.79) * mm});
            skArc(sketch, "E227.MirrorCS", {"start": v(272.67, -76.78) * mm, "mid": v(272.89, -75.97) * mm, "end": v(273.65, -75.62) * mm});
            skLineSegment(sketch, "E228.MirrorCS", {"start": v(276, -91.02) * mm, "end": v(278.39, -91.02) * mm});
            skArc(sketch, "E229.MirrorCS", {"start": v(276, -91.02) * mm, "mid": v(275.37, -90.79) * mm, "end": v(275.03, -90.2) * mm});
            skArc(sketch, "E230.MirrorCS", {"start": v(279.36, -90.2) * mm, "mid": v(279.02, -90.78) * mm, "end": v(278.39, -91.02) * mm});
            skArc(sketch, "E231.MirrorCS", {"start": v(280.75, -75.68) * mm, "mid": v(281.5, -76.04) * mm, "end": v(281.72, -76.84) * mm});
            skLineSegment(sketch, "E232.MirrorCS", {"start": v(280.75, -75.68) * mm, "end": v(273.65, -75.62) * mm});
            skLineSegment(sketch, "E233.MirrorCS", {"start": v(272.67, -76.78) * mm, "end": v(275.03, -90.2) * mm});
            skLineSegment(sketch, "E234.MirrorCS", {"start": v(279.36, -90.2) * mm, "end": v(281.72, -76.84) * mm});
            skSolve(sketch);
        }
        {
            var Q0;
            Q0=makeQuery(id+"F0.imprint","IMPRINT",FACE,{"disambiguationData":[TD([[makeQuery(id+"F0.imprint","IMPRINT",EDGE,{"derivedFrom":sQuery(id+"F0.wireOp",EDGE,"E0")}),1.0]])]});
            var Q1;
            Q1=makeQuery(id+"F2.imprint","IMPRINT",FACE,{"disambiguationData":[TD([[makeQuery(id+"F2.imprint","IMPRINT",EDGE,{"derivedFrom":sQuery(id+"F2.wireOp",EDGE,"E10.0")}),-1.0]])]});
            var Q2;
            Q2=makeQuery(id+"F2.imprint","IMPRINT",FACE,{"disambiguationData":[TD([[makeQuery(id+"F2.imprint","IMPRINT",EDGE,{"derivedFrom":sQuery(id+"F2.wireOp",EDGE,"E22.0")}),-1.0]])]});
            var Q3;
            Q3=makeQuery(id+"F2.imprint","IMPRINT",FACE,{"disambiguationData":[TD([[makeQuery(id+"F2.imprint","IMPRINT",EDGE,{"derivedFrom":sQuery(id+"F2.wireOp",EDGE,"E4.0")}),-1.0]])]});
            var Q4;
            Q4=makeQuery(id+"F2.imprint","IMPRINT",FACE,{"disambiguationData":[TD([[makeQuery(id+"F2.imprint","IMPRINT",EDGE,{"derivedFrom":sQuery(id+"F2.wireOp",EDGE,"E32.0")}),-1.0]])]});
            var Q5;
            Q5=makeQuery(id+"F2.imprint","IMPRINT",FACE,{"disambiguationData":[TD([[makeQuery(id+"F2.imprint","IMPRINT",EDGE,{"derivedFrom":sQuery(id+"F2.wireOp",EDGE,"E27.2.0")}),-1.0]])]});
            var Q6;
            Q6=makeQuery(id+"F2.imprint","IMPRINT",FACE,{"disambiguationData":[TD([[makeQuery(id+"F2.imprint","IMPRINT",EDGE,{"derivedFrom":sQuery(id+"F2.wireOp",EDGE,"E15.2.0")}),-1.0]])]});
            var Q7;
            Q7=makeQuery(id+"F2.imprint","IMPRINT",FACE,{"disambiguationData":[TD([[makeQuery(id+"F2.imprint","IMPRINT",EDGE,{"derivedFrom":sQuery(id+"F2.wireOp",EDGE,"E9.2.0")}),-1.0]])]});
            var Q8;
            Q8=makeQuery(id+"F2.imprint","IMPRINT",FACE,{"disambiguationData":[TD([[makeQuery(id+"F2.imprint","IMPRINT",EDGE,{"derivedFrom":sQuery(id+"F2.wireOp",EDGE,"E21.2.0")}),-1.0]])]});
            var Q9;
            Q9=makeQuery(id+"F2.imprint","IMPRINT",FACE,{"disambiguationData":[TD([[makeQuery(id+"F2.imprint","IMPRINT",EDGE,{"derivedFrom":sQuery(id+"F2.wireOp",EDGE,"E50.2.0")}),-1.0]])]});
            var Q10;
            Q10=makeQuery(id+"F2.imprint","IMPRINT",FACE,{"disambiguationData":[TD([[makeQuery(id+"F2.imprint","IMPRINT",EDGE,{"derivedFrom":sQuery(id+"F2.wireOp",EDGE,"E51.MirrorCS")}),1.0]])]});
            var Q11;
            Q11=makeQuery(id+"F2.imprint","IMPRINT",FACE,{"disambiguationData":[TD([[makeQuery(id+"F2.imprint","IMPRINT",EDGE,{"derivedFrom":sQuery(id+"F2.wireOp",EDGE,"E107.MirrorCS")}),-1.0]])]});
            var Q12;
            Q12=makeQuery(id+"F2.imprint","IMPRINT",FACE,{"disambiguationData":[TD([[makeQuery(id+"F2.imprint","IMPRINT",EDGE,{"derivedFrom":sQuery(id+"F2.wireOp",EDGE,"E115.MirrorCS")}),-1.0]])]});
            var Q13;
            Q13=makeQuery(id+"F2.imprint","IMPRINT",FACE,{"disambiguationData":[TD([[makeQuery(id+"F2.imprint","IMPRINT",EDGE,{"derivedFrom":sQuery(id+"F2.wireOp",EDGE,"E123.MirrorCS")}),-1.0]])]});
            var Q14;
            Q14=makeQuery(id+"F2.imprint","IMPRINT",FACE,{"disambiguationData":[TD([[makeQuery(id+"F2.imprint","IMPRINT",EDGE,{"derivedFrom":sQuery(id+"F2.wireOp",EDGE,"E137.MirrorCS")}),1.0]])]});
            var Q15;
            Q15=makeQuery(id+"F2.imprint","IMPRINT",FACE,{"disambiguationData":[TD([[makeQuery(id+"F2.imprint","IMPRINT",EDGE,{"derivedFrom":sQuery(id+"F2.wireOp",EDGE,"E135.MirrorCS")}),1.0]])]});
            var Q16;
            Q16=makeQuery(id+"F2.imprint","IMPRINT",FACE,{"disambiguationData":[TD([[makeQuery(id+"F2.imprint","IMPRINT",EDGE,{"derivedFrom":sQuery(id+"F2.wireOp",EDGE,"E134.MirrorCS")}),-1.0]])]});
            var Q17;
            Q17=makeQuery(id+"F2.imprint","IMPRINT",FACE,{"disambiguationData":[TD([[makeQuery(id+"F2.imprint","IMPRINT",EDGE,{"derivedFrom":sQuery(id+"F2.wireOp",EDGE,"E49.2.0")}),-1.0]])]});
            var Q18;
            Q18=makeQuery(id+"F2.imprint","IMPRINT",FACE,{"disambiguationData":[TD([[makeQuery(id+"F2.imprint","IMPRINT",EDGE,{"derivedFrom":sQuery(id+"F2.wireOp",EDGE,"E59.MirrorCS")}),-1.0]])]});
            var Q19;
            Q19=makeQuery(id+"F2.imprint","IMPRINT",FACE,{"disambiguationData":[TD([[makeQuery(id+"F2.imprint","IMPRINT",EDGE,{"derivedFrom":sQuery(id+"F2.wireOp",EDGE,"E67.MirrorCS")}),-1.0]])]});
            var Q20;
            Q20=makeQuery(id+"F2.imprint","IMPRINT",FACE,{"disambiguationData":[TD([[makeQuery(id+"F2.imprint","IMPRINT",EDGE,{"derivedFrom":sQuery(id+"F2.wireOp",EDGE,"E75.MirrorCS")}),-1.0]])]});
            var Q21;
            Q21=makeQuery(id+"F2.imprint","IMPRINT",FACE,{"disambiguationData":[TD([[makeQuery(id+"F2.imprint","IMPRINT",EDGE,{"derivedFrom":sQuery(id+"F2.wireOp",EDGE,"E83.MirrorCS")}),-1.0]])]});
            var Q22;
            Q22=makeQuery(id+"F2.imprint","IMPRINT",FACE,{"disambiguationData":[TD([[makeQuery(id+"F2.imprint","IMPRINT",EDGE,{"derivedFrom":sQuery(id+"F2.wireOp",EDGE,"E91.MirrorCS")}),1.0]])]});
            var Q23;
            Q23=makeQuery(id+"F2.imprint","IMPRINT",FACE,{"disambiguationData":[TD([[makeQuery(id+"F2.imprint","IMPRINT",EDGE,{"derivedFrom":sQuery(id+"F2.wireOp",EDGE,"E99.MirrorCS")}),1.0]])]});
            var Q24;
            Q24=makeQuery(id+"F2.imprint","IMPRINT",FACE,{"disambiguationData":[TD([[makeQuery(id+"F2.imprint","IMPRINT",EDGE,{"derivedFrom":sQuery(id+"F2.wireOp",EDGE,"E31.2.0")}),-1.0]])]});
            var Q25;
            Q25=makeQuery(id+"F2.imprint","IMPRINT",FACE,{"disambiguationData":[TD([[makeQuery(id+"F2.imprint","IMPRINT",EDGE,{"derivedFrom":sQuery(id+"F2.wireOp",EDGE,"E37.2.0")}),-1.0]])]});
            var Q26;
            Q26=makeQuery(id+"F2.imprint","IMPRINT",FACE,{"disambiguationData":[TD([[makeQuery(id+"F2.imprint","IMPRINT",EDGE,{"derivedFrom":sQuery(id+"F2.wireOp",EDGE,"E44.0")}),-1.0]])]});
            var Q27;
            Q27=makeQuery(id+"F2.imprint","IMPRINT",FACE,{"disambiguationData":[TD([[makeQuery(id+"F2.imprint","IMPRINT",EDGE,{"derivedFrom":sQuery(id+"F2.wireOp",EDGE,"E38.0")}),-1.0]])]});
            var Q28;
            Q28=makeQuery(id+"F2.imprint","IMPRINT",FACE,{"disambiguationData":[TD([[makeQuery(id+"F2.imprint","IMPRINT",EDGE,{"derivedFrom":sQuery(id+"F2.wireOp",EDGE,"E16.0")}),-1.0]])]});
            extrude(context, id + "F3", {"entities" : qUnion([Q0, Q1, Q2, Q3, Q4, Q5, Q6, Q7, Q8, Q9, Q10, Q11, Q12, Q13, Q14, Q15, Q16, Q17, Q18, Q19, Q20, Q21, Q22, Q23, Q24, Q25, Q26, Q27, Q28]), "depth" : 12.7 * mm});
        }
        {
            var Q0;
            Q0=makeQuery(id+"F2.imprint","IMPRINT",FACE,{"disambiguationData":[TD([[makeQuery(id+"F2.imprint","IMPRINT",EDGE,{"derivedFrom":sQuery(id+"F2.wireOp",EDGE,"E155.MirrorCS")}),-1.0]])]});
            var Q1;
            Q1=makeQuery(id+"F2.imprint","IMPRINT",FACE,{"disambiguationData":[TD([[makeQuery(id+"F2.imprint","IMPRINT",EDGE,{"derivedFrom":sQuery(id+"F2.wireOp",EDGE,"E30.2.0")}),-1.0]])]});
            var Q2;
            Q2=makeQuery(id+"F2.imprint","IMPRINT",FACE,{"disambiguationData":[TD([[makeQuery(id+"F2.imprint","IMPRINT",EDGE,{"derivedFrom":sQuery(id+"F2.wireOp",EDGE,"E28.2.0")}),-1.0]])]});
            var Q3;
            Q3=makeQuery(id+"F2.imprint","IMPRINT",FACE,{"disambiguationData":[TD([[makeQuery(id+"F2.imprint","IMPRINT",EDGE,{"derivedFrom":sQuery(id+"F2.wireOp",EDGE,"E29.2.0")}),-1.0]])]});
            var Q4;
            Q4=makeQuery(id+"F2.imprint","IMPRINT",FACE,{"disambiguationData":[TD([[makeQuery(id+"F2.imprint","IMPRINT",EDGE,{"derivedFrom":sQuery(id+"F2.wireOp",EDGE,"E43.2.0")}),-1.0]])]});
            var Q5;
            Q5=makeQuery(id+"F2.imprint","IMPRINT",FACE,{"disambiguationData":[TD([[makeQuery(id+"F2.imprint","IMPRINT",EDGE,{"derivedFrom":sQuery(id+"F2.wireOp",EDGE,"E203.MirrorCS")}),-1.0]])]});
            var Q6;
            Q6=makeQuery(id+"F2.imprint","IMPRINT",FACE,{"disambiguationData":[TD([[makeQuery(id+"F2.imprint","IMPRINT",EDGE,{"derivedFrom":sQuery(id+"F2.wireOp",EDGE,"E206.MirrorCS")}),-1.0]])]});
            var Q7;
            Q7=makeQuery(id+"F2.imprint","IMPRINT",FACE,{"disambiguationData":[TD([[makeQuery(id+"F2.imprint","IMPRINT",EDGE,{"derivedFrom":sQuery(id+"F2.wireOp",EDGE,"E210.MirrorCS")}),-1.0]])]});
            var Q8;
            Q8=makeQuery(id+"F2.imprint","IMPRINT",FACE,{"disambiguationData":[TD([[makeQuery(id+"F2.imprint","IMPRINT",EDGE,{"derivedFrom":sQuery(id+"F2.wireOp",EDGE,"E227.MirrorCS")}),-1.0]])]});
            var Q9;
            Q9=makeQuery(id+"F2.imprint","IMPRINT",FACE,{"disambiguationData":[TD([[makeQuery(id+"F2.imprint","IMPRINT",EDGE,{"derivedFrom":sQuery(id+"F2.wireOp",EDGE,"E188.MirrorCS")}),1.0]])]});
            var Q10;
            Q10=makeQuery(id+"F2.imprint","IMPRINT",FACE,{"disambiguationData":[TD([[makeQuery(id+"F2.imprint","IMPRINT",EDGE,{"derivedFrom":sQuery(id+"F2.wireOp",EDGE,"E180.MirrorCS")}),1.0]])]});
            var Q11;
            Q11=makeQuery(id+"F2.imprint","IMPRINT",FACE,{"disambiguationData":[TD([[makeQuery(id+"F2.imprint","IMPRINT",EDGE,{"derivedFrom":sQuery(id+"F2.wireOp",EDGE,"E179.MirrorCS")}),1.0]])]});
            var Q12;
            Q12=makeQuery(id+"F2.imprint","IMPRINT",FACE,{"disambiguationData":[TD([[makeQuery(id+"F2.imprint","IMPRINT",EDGE,{"derivedFrom":sQuery(id+"F2.wireOp",EDGE,"E157.MirrorCS")}),1.0]])]});
            var Q13;
            Q13=makeQuery(id+"F2.imprint","IMPRINT",FACE,{"disambiguationData":[TD([[makeQuery(id+"F2.imprint","IMPRINT",EDGE,{"derivedFrom":sQuery(id+"F2.wireOp",EDGE,"E159.MirrorCS")}),-1.0]])]});
            var Q14;
            Q14=makeQuery(id+"F1.imprint","IMPRINT",FACE,{"disambiguationData":[TD([[makeQuery(id+"F1.imprint","IMPRINT",EDGE,{"derivedFrom":sQuery(id+"F1.wireOp",EDGE,"E2")}),1.0]])]});
            extrude(context, id + "F4", {"entities" : qUnion([Q0, Q1, Q2, Q3, Q4, Q5, Q6, Q7, Q8, Q9, Q10, Q11, Q12, Q13, Q14]), "depth" : 6.35 * mm});
        }
    });
